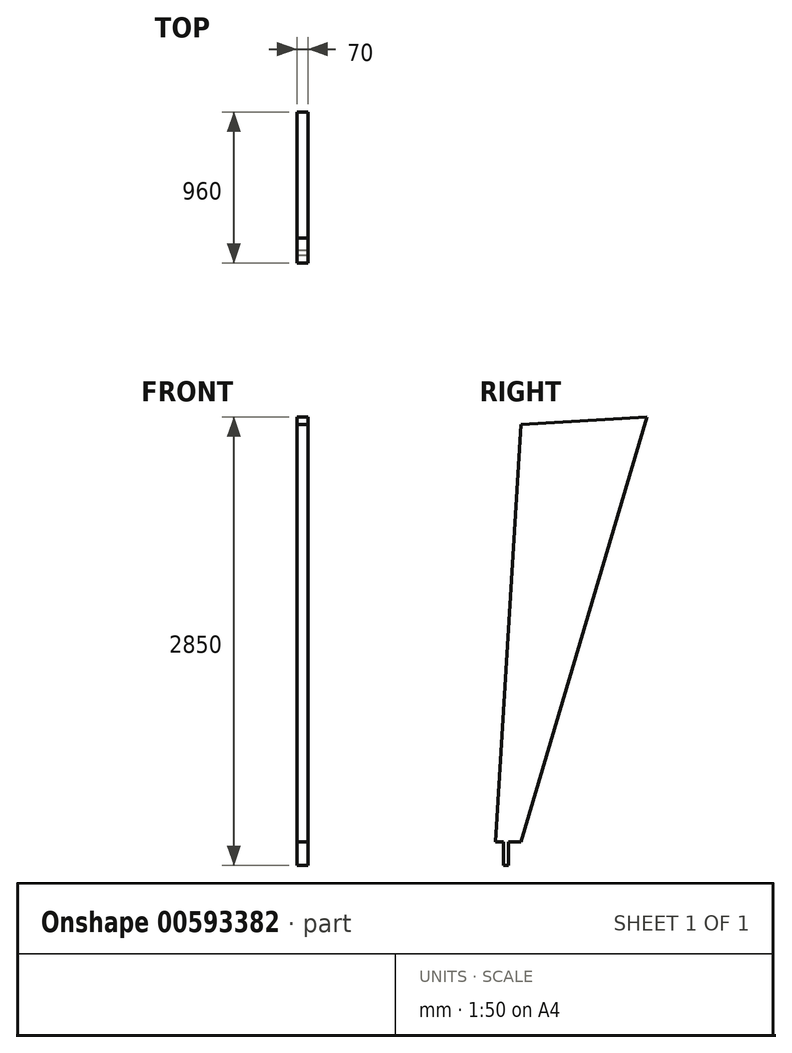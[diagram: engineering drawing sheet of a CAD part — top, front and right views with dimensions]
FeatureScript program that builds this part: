
annotation { "Feature Type Name" : "Feature", "Feature Type Description" : "" }
export const myFeature = defineFeature(function(context is Context, id is Id, definition is map)
    precondition{}
    {
        {
            var Q0;
            Q0=qCreatedBy(makeId("Right.planeOp"),FACE);
            var sketch = newSketch(context, id + "F0", { "sketchPlane" : qUnion([Q0])});
            skLineSegment(sketch, "E0.top", {"start": v(-497.93, -1145.42) * mm, "end": v(-467.93, -1145.42) * mm});
            skLineSegment(sketch, "E0.left", {"start": v(-497.93, -995.42) * mm, "end": v(-497.93, -1145.42) * mm});
            skLineSegment(sketch, "E0.right", {"start": v(-467.93, -995.42) * mm, "end": v(-467.93, -1145.42) * mm});
            skLineSegment(sketch, "E1", {"start": v(-467.93, -995.42) * mm, "end": v(-387.93, -995.42) * mm});
            skLineSegment(sketch, "E2", {"start": v(-387.93, -995.42) * mm, "end": v(412.07, 1704.58) * mm});
            skLineSegment(sketch, "E3", {"start": v(412.07, 1704.58) * mm, "end": v(-387.93, 1654.58) * mm});
            skLineSegment(sketch, "E4", {"start": v(-387.93, 1654.58) * mm, "end": v(-547.93, -995.42) * mm});
            skLineSegment(sketch, "E5", {"start": v(-547.93, -995.42) * mm, "end": v(-497.93, -995.42) * mm});
            skLineSegment(sketch, "E6", {"start": v(-387.93, -995.42) * mm, "end": v(-387.93, 1654.58) * mm, "construction": true});
            skLineSegment(sketch, "E7", {"start": v(-387.93, -995.42) * mm, "end": v(412.07, -995.42) * mm, "construction": true});
            skLineSegment(sketch, "E8", {"start": v(412.07, -995.42) * mm, "end": v(412.07, 1704.58) * mm, "construction": true});
            skSolve(sketch);
        }
        {
            var Q0;
            Q0 = qSketchRegion(id + "F0", true);
            extrude(context, id + "F1", {"entities" : qUnion([Q0]), "depth" : 70 * mm, "offsetDistance" : 25 * mm});
        }
    });
